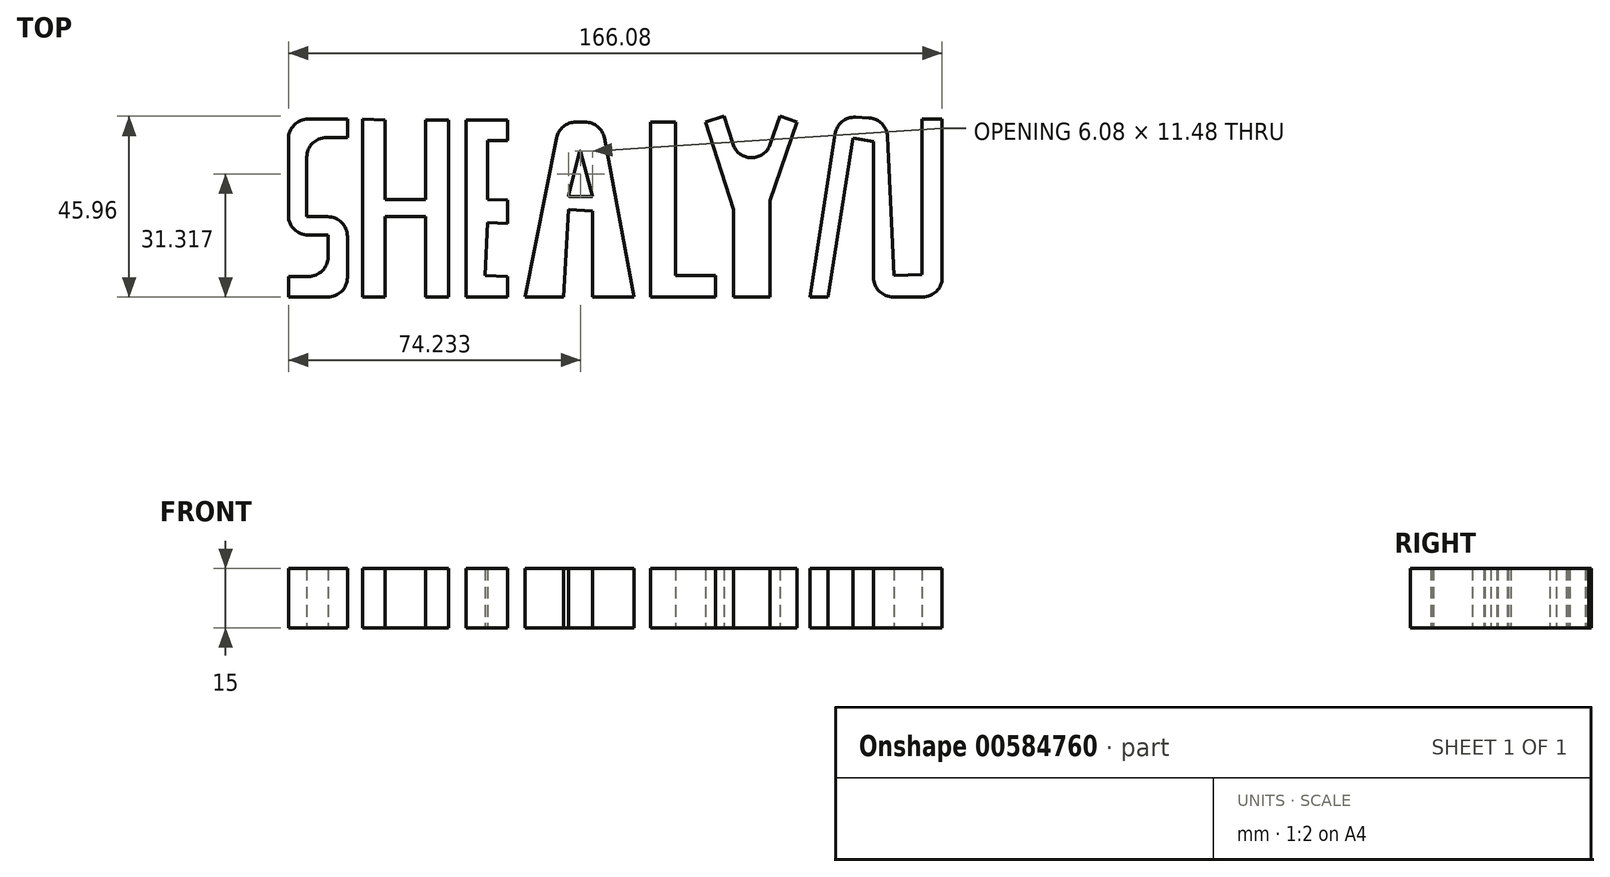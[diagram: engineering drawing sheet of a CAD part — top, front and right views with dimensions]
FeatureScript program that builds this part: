
annotation { "Feature Type Name" : "Feature", "Feature Type Description" : "" }
export const myFeature = defineFeature(function(context is Context, id is Id, definition is map)
    precondition{}
    {
        {
            var Q0;
            Q0=qCreatedBy(makeId("Top.planeOp"),FACE);
            var sketch = newSketch(context, id + "F0", { "sketchPlane" : qUnion([Q0])});
            skLineSegment(sketch, "E0", {"start": v(-66.67, 40.54) * mm, "end": v(-71.97, 40.54) * mm});
            skLineSegment(sketch, "E1", {"start": v(-76.97, 35.54) * mm, "end": v(-76.97, 20.42) * mm});
            skLineSegment(sketch, "E2", {"start": v(-76.97, 20.42) * mm, "end": v(-71.67, 20.42) * mm});
            skLineSegment(sketch, "E3", {"start": v(-66.67, 15.42) * mm, "end": v(-66.67, 5) * mm});
            skLineSegment(sketch, "E4", {"start": v(-71.67, 0) * mm, "end": v(-76.97, 0) * mm});
            skLineSegment(sketch, "E5", {"start": v(-76.97, 5.21) * mm, "end": v(-76.57, 5.21) * mm});
            skLineSegment(sketch, "E6", {"start": v(-71.57, 10.21) * mm, "end": v(-71.57, 15.76) * mm});
            skLineSegment(sketch, "E7", {"start": v(-71.57, 15.76) * mm, "end": v(-76.63, 15.76) * mm});
            skLineSegment(sketch, "E8", {"start": v(-81.63, 20.76) * mm, "end": v(-81.63, 40.2) * mm});
            skLineSegment(sketch, "E9", {"start": v(-76.63, 45.2) * mm, "end": v(-66.67, 45.2) * mm});
            skLineSegment(sketch, "E10", {"start": v(-66.67, 45.2) * mm, "end": v(-66.67, 40.54) * mm});
            skLineSegment(sketch, "E11", {"start": v(-81.63, 5.21) * mm, "end": v(-81.63, 0) * mm});
            skLineSegment(sketch, "E12", {"start": v(-81.63, 0) * mm, "end": v(-76.97, 0) * mm});
            skLineSegment(sketch, "E13", {"start": v(-76.97, 5.21) * mm, "end": v(-81.63, 5.21) * mm});
            skLineSegment(sketch, "E14", {"start": v(-62.74, 45.2) * mm, "end": v(-62.74, 0) * mm});
            skLineSegment(sketch, "E15", {"start": v(-62.74, 0) * mm, "end": v(-57.1, 0) * mm});
            skLineSegment(sketch, "E16", {"start": v(-57.1, 0) * mm, "end": v(-57.1, 20.42) * mm});
            skLineSegment(sketch, "E17", {"start": v(-57.1, 20.42) * mm, "end": v(-46.8, 20.42) * mm});
            skLineSegment(sketch, "E18", {"start": v(-46.8, 20.42) * mm, "end": v(-46.8, 0) * mm});
            skLineSegment(sketch, "E19", {"start": v(-46.8, 0) * mm, "end": v(-40.9, 0) * mm});
            skLineSegment(sketch, "E20", {"start": v(-40.9, 0) * mm, "end": v(-40.9, 24.84) * mm});
            skLineSegment(sketch, "E21", {"start": v(-57.1, 24.84) * mm, "end": v(-57.1, 44.96) * mm});
            skLineSegment(sketch, "E22", {"start": v(-57.1, 44.96) * mm, "end": v(-62.74, 45.2) * mm});
            skLineSegment(sketch, "E23", {"start": v(-36.5, 0) * mm, "end": v(-36.5, 44.96) * mm});
            skLineSegment(sketch, "E24", {"start": v(-36.5, 44.96) * mm, "end": v(-25.94, 44.96) * mm});
            skLineSegment(sketch, "E25", {"start": v(-25.94, 44.96) * mm, "end": v(-25.94, 39.8) * mm});
            skLineSegment(sketch, "E26", {"start": v(-25.94, 39.8) * mm, "end": v(-31.1, 39.8) * mm});
            skLineSegment(sketch, "E27", {"start": v(-31.1, 39.8) * mm, "end": v(-31.1, 24.84) * mm});
            skLineSegment(sketch, "E28", {"start": v(-31.1, 24.84) * mm, "end": v(-25.94, 24.62) * mm});
            skLineSegment(sketch, "E29", {"start": v(-25.94, 24.62) * mm, "end": v(-25.94, 18.7) * mm});
            skLineSegment(sketch, "E30", {"start": v(-25.94, 18.7) * mm, "end": v(-31.1, 18.93) * mm});
            skLineSegment(sketch, "E31", {"start": v(-31.1, 18.93) * mm, "end": v(-31.68, 5.5) * mm});
            skLineSegment(sketch, "E32", {"start": v(-31.68, 5.5) * mm, "end": v(-25.94, 5.25) * mm});
            skLineSegment(sketch, "E33", {"start": v(-25.94, 5.25) * mm, "end": v(-25.94, 0) * mm});
            skLineSegment(sketch, "E34", {"start": v(-25.94, 0) * mm, "end": v(-36.5, 0) * mm});
            skLineSegment(sketch, "E35", {"start": v(-21.53, 0) * mm, "end": v(-13.5, 40.44) * mm});
            skLineSegment(sketch, "E36", {"start": v(-8.6, 44.47) * mm, "end": v(-6.3, 44.47) * mm});
            skLineSegment(sketch, "E37", {"start": v(-1.38, 40.39) * mm, "end": v(6.2, 0) * mm});
            skLineSegment(sketch, "E38", {"start": v(6.2, 0) * mm, "end": v(-4.35, 0) * mm});
            skLineSegment(sketch, "E39", {"start": v(-4.35, 0) * mm, "end": v(-4.35, 21.9) * mm});
            skLineSegment(sketch, "E40", {"start": v(-4.35, 21.9) * mm, "end": v(-10.49, 22.23) * mm});
            skPoint(sketch, "E40.endSnap0", {"position": v(-17.11, 22.23) * mm});
            skLineSegment(sketch, "E41", {"start": v(-10.49, 22.23) * mm, "end": v(-11.71, 0) * mm});
            skLineSegment(sketch, "E42", {"start": v(-11.71, 0) * mm, "end": v(-21.53, 0) * mm});
            skLineSegment(sketch, "E43", {"start": v(-7.7, 36.92) * mm, "end": v(-10.43, 25.8) * mm});
            skLineSegment(sketch, "E44", {"start": v(-10.26, 25.58) * mm, "end": v(-4.35, 25.58) * mm});
            skLineSegment(sketch, "E45", {"start": v(-4.35, 25.58) * mm, "end": v(-7.37, 36.93) * mm});
            skLineSegment(sketch, "E46", {"start": v(10.37, 0) * mm, "end": v(10.37, 44.47) * mm});
            skPoint(sketch, "E46.endSnap0", {"position": v(-7.42, 44.47) * mm});
            skLineSegment(sketch, "E47", {"start": v(10.37, 44.47) * mm, "end": v(16.74, 44.47) * mm});
            skLineSegment(sketch, "E48", {"start": v(16.74, 44.47) * mm, "end": v(16.74, 5.46) * mm});
            skLineSegment(sketch, "E49", {"start": v(16.74, 5.46) * mm, "end": v(26.8, 5.46) * mm});
            skLineSegment(sketch, "E50", {"start": v(26.8, 5.46) * mm, "end": v(26.8, 0) * mm});
            skLineSegment(sketch, "E51", {"start": v(26.8, 0) * mm, "end": v(10.37, 0) * mm});
            skPoint(sketch, "E52.endSnap0", {"position": v(2.02, 22.23) * mm});
            skLineSegment(sketch, "E53", {"start": v(31.46, 0) * mm, "end": v(31.46, 22.23) * mm});
            skLineSegment(sketch, "E54", {"start": v(31.46, 22.23) * mm, "end": v(24.35, 44.47) * mm});
            skLineSegment(sketch, "E55", {"start": v(24.35, 44.47) * mm, "end": v(29.01, 45.96) * mm});
            skLineSegment(sketch, "E56", {"start": v(29.01, 45.96) * mm, "end": v(31.27, 38.9) * mm});
            skLineSegment(sketch, "E57", {"start": v(40.76, 38.79) * mm, "end": v(43.24, 45.96) * mm});
            skLineSegment(sketch, "E58", {"start": v(43.24, 45.96) * mm, "end": v(47.56, 44.47) * mm});
            skLineSegment(sketch, "E59", {"start": v(47.56, 44.47) * mm, "end": v(40.7, 24.58) * mm});
            skLineSegment(sketch, "E60", {"start": v(40.7, 24.58) * mm, "end": v(40.7, 0) * mm});
            skLineSegment(sketch, "E61", {"start": v(40.7, 0) * mm, "end": v(31.46, 0) * mm});
            skLineSegment(sketch, "E62", {"start": v(47.56, 44.47) * mm, "end": v(43.24, 45.96) * mm});
            skLineSegment(sketch, "E63", {"start": v(50.84, 0) * mm, "end": v(57.27, 41.48) * mm});
            skLineSegment(sketch, "E64", {"start": v(62.48, 45.7) * mm, "end": v(64.6, 45.6) * mm});
            skLineSegment(sketch, "E65", {"start": v(64.6, 45.6) * mm, "end": v(65.88, 45.52) * mm});
            skLineSegment(sketch, "E66", {"start": v(70.6, 40.76) * mm, "end": v(72.19, 5.46) * mm});
            skLineSegment(sketch, "E67", {"start": v(72.19, 5.46) * mm, "end": v(79.33, 5.78) * mm});
            skLineSegment(sketch, "E68", {"start": v(79.33, 5.78) * mm, "end": v(79.33, 45.27) * mm});
            skLineSegment(sketch, "E69", {"start": v(79.33, 45.27) * mm, "end": v(84.45, 45.27) * mm});
            skLineSegment(sketch, "E70", {"start": v(84.45, 45.27) * mm, "end": v(84.45, 5) * mm});
            skLineSegment(sketch, "E71", {"start": v(79.45, 0) * mm, "end": v(72.04, 0) * mm});
            skLineSegment(sketch, "E72", {"start": v(67.04, 5) * mm, "end": v(67.04, 39.56) * mm});
            skLineSegment(sketch, "E73", {"start": v(67.04, 39.56) * mm, "end": v(61.73, 40.38) * mm});
            skLineSegment(sketch, "E74", {"start": v(61.73, 40.38) * mm, "end": v(55.48, 0) * mm});
            skLineSegment(sketch, "E75", {"start": v(55.48, 0) * mm, "end": v(50.84, 0) * mm});
            skLineSegment(sketch, "E76", {"start": v(-57.1, 24.84) * mm, "end": v(-46.8, 24.84) * mm});
            skLineSegment(sketch, "E77", {"start": v(-46.8, 24.84) * mm, "end": v(-46.8, 44.96) * mm});
            skLineSegment(sketch, "E78", {"start": v(-46.8, 44.96) * mm, "end": v(-40.9, 44.96) * mm});
            skLineSegment(sketch, "E79", {"start": v(-40.9, 44.96) * mm, "end": v(-40.9, 24.84) * mm});
            skPoint(sketch, "E80.visualSharp", {"position": v(-66.67, 20.42) * mm});
            skArc(sketch, "E80.filletArc", {"start": v(-66.67, 15.42) * mm, "mid": v(-68.13, 18.96) * mm, "end": v(-71.67, 20.42) * mm});
            skPoint(sketch, "E81.visualSharp", {"position": v(-66.67, 0) * mm});
            skArc(sketch, "E81.filletArc", {"start": v(-71.67, 0) * mm, "mid": v(-68.13, 1.46) * mm, "end": v(-66.67, 5) * mm});
            skPoint(sketch, "E82.visualSharp", {"position": v(-81.63, 45.2) * mm});
            skArc(sketch, "E82.filletArc", {"start": v(-76.63, 45.2) * mm, "mid": v(-80.17, 43.74) * mm, "end": v(-81.63, 40.2) * mm});
            skPoint(sketch, "E83.visualSharp", {"position": v(-2.15, 44.47) * mm});
            skArc(sketch, "E83.filletArc", {"start": v(-1.38, 40.39) * mm, "mid": v(-3.1, 43.31) * mm, "end": v(-6.3, 44.47) * mm});
            skPoint(sketch, "E84.visualSharp", {"position": v(-12.7, 44.47) * mm});
            skArc(sketch, "E84.filletArc", {"start": v(-8.6, 44.47) * mm, "mid": v(-11.76, 43.33) * mm, "end": v(-13.5, 40.44) * mm});
            skPoint(sketch, "E85.visualSharp", {"position": v(70.4, 45.27) * mm});
            skArc(sketch, "E85.filletArc", {"start": v(70.6, 40.76) * mm, "mid": v(69.15, 44.05) * mm, "end": v(65.88, 45.52) * mm});
            skPoint(sketch, "E86.visualSharp", {"position": v(57.96, 45.96) * mm});
            skArc(sketch, "E86.filletArc", {"start": v(62.48, 45.7) * mm, "mid": v(59.06, 44.6) * mm, "end": v(57.27, 41.48) * mm});
            skPoint(sketch, "E87.visualSharp", {"position": v(67.04, 0) * mm});
            skArc(sketch, "E87.filletArc", {"start": v(67.04, 5) * mm, "mid": v(68.5, 1.46) * mm, "end": v(72.04, 0) * mm});
            skPoint(sketch, "E88.visualSharp", {"position": v(84.45, 0) * mm});
            skArc(sketch, "E88.filletArc", {"start": v(79.45, 0) * mm, "mid": v(82.99, 1.46) * mm, "end": v(84.45, 5) * mm});
            skPoint(sketch, "E89.visualSharp", {"position": v(-71.57, 5.21) * mm});
            skArc(sketch, "E89.filletArc", {"start": v(-76.57, 5.21) * mm, "mid": v(-73.04, 6.68) * mm, "end": v(-71.57, 10.21) * mm});
            skPoint(sketch, "E90.visualSharp", {"position": v(-76.97, 40.54) * mm});
            skArc(sketch, "E90.filletArc", {"start": v(-71.97, 40.54) * mm, "mid": v(-75.5, 39.08) * mm, "end": v(-76.97, 35.54) * mm});
            skPoint(sketch, "E91.visualSharp", {"position": v(-7.54, 37.6) * mm});
            skArc(sketch, "E91.filletArc", {"start": v(-7.37, 36.93) * mm, "mid": v(-7.54, 37.06) * mm, "end": v(-7.7, 36.92) * mm});
            skPoint(sketch, "E92.visualSharp", {"position": v(-10.49, 25.58) * mm});
            skArc(sketch, "E92.filletArc", {"start": v(-10.43, 25.8) * mm, "mid": v(-10.4, 25.64) * mm, "end": v(-10.26, 25.58) * mm});
            skPoint(sketch, "E93.visualSharp", {"position": v(-81.63, 15.76) * mm});
            skArc(sketch, "E93.filletArc", {"start": v(-81.63, 20.76) * mm, "mid": v(-80.17, 17.23) * mm, "end": v(-76.63, 15.76) * mm});
            skPoint(sketch, "E94.visualSharp", {"position": v(35.86, 24.58) * mm});
            skArc(sketch, "E94.filletArc", {"start": v(31.27, 38.9) * mm, "mid": v(35.98, 35.42) * mm, "end": v(40.76, 38.79) * mm});
            skSolve(sketch);
        }
        {
            var Q0;
            Q0=makeQuery(id+"F0.imprint","IMPRINT",FACE,{"disambiguationData":[TD([[makeQuery(id+"F0.imprint","IMPRINT",EDGE,{"derivedFrom":sQuery(id+"F0.wireOp",EDGE,"E0")}),-1.0]])]});
            var Q1;
            Q1=makeQuery(id+"F0.imprint","IMPRINT",FACE,{"disambiguationData":[TD([[makeQuery(id+"F0.imprint","IMPRINT",EDGE,{"derivedFrom":sQuery(id+"F0.wireOp",EDGE,"E14")}),1.0]])]});
            var Q2;
            Q2=makeQuery(id+"F0.imprint","IMPRINT",FACE,{"disambiguationData":[TD([[makeQuery(id+"F0.imprint","IMPRINT",EDGE,{"derivedFrom":sQuery(id+"F0.wireOp",EDGE,"E23")}),-1.0]])]});
            var Q3;
            Q3=makeQuery(id+"F0.imprint","IMPRINT",FACE,{"disambiguationData":[TD([[makeQuery(id+"F0.imprint","IMPRINT",EDGE,{"derivedFrom":sQuery(id+"F0.wireOp",EDGE,"E46")}),-1.0]])]});
            var Q4;
            Q4=makeQuery(id+"F0.imprint","IMPRINT",FACE,{"disambiguationData":[TD([[makeQuery(id+"F0.imprint","IMPRINT",EDGE,{"derivedFrom":sQuery(id+"F0.wireOp",EDGE,"E53")}),-1.0]])]});
            var Q5;
            Q5=makeQuery(id+"F0.imprint","IMPRINT",FACE,{"disambiguationData":[TD([[makeQuery(id+"F0.imprint","IMPRINT",EDGE,{"derivedFrom":sQuery(id+"F0.wireOp",EDGE,"E63")}),-1.0]])]});
            var Q6;
            Q6=makeQuery(id+"F0.imprint","IMPRINT",FACE,{"disambiguationData":[TD([[makeQuery(id+"F0.imprint","IMPRINT",EDGE,{"derivedFrom":sQuery(id+"F0.wireOp",EDGE,"E35")}),-1.0]])]});
            extrude(context, id + "F1", {"entities" : qUnion([Q0, Q1, Q2, Q3, Q4, Q5, Q6]), "endBound" : BoundingType.SYMMETRIC, "depth" : 15 * mm, "offsetDistance" : 25 * mm});
        }
    });
